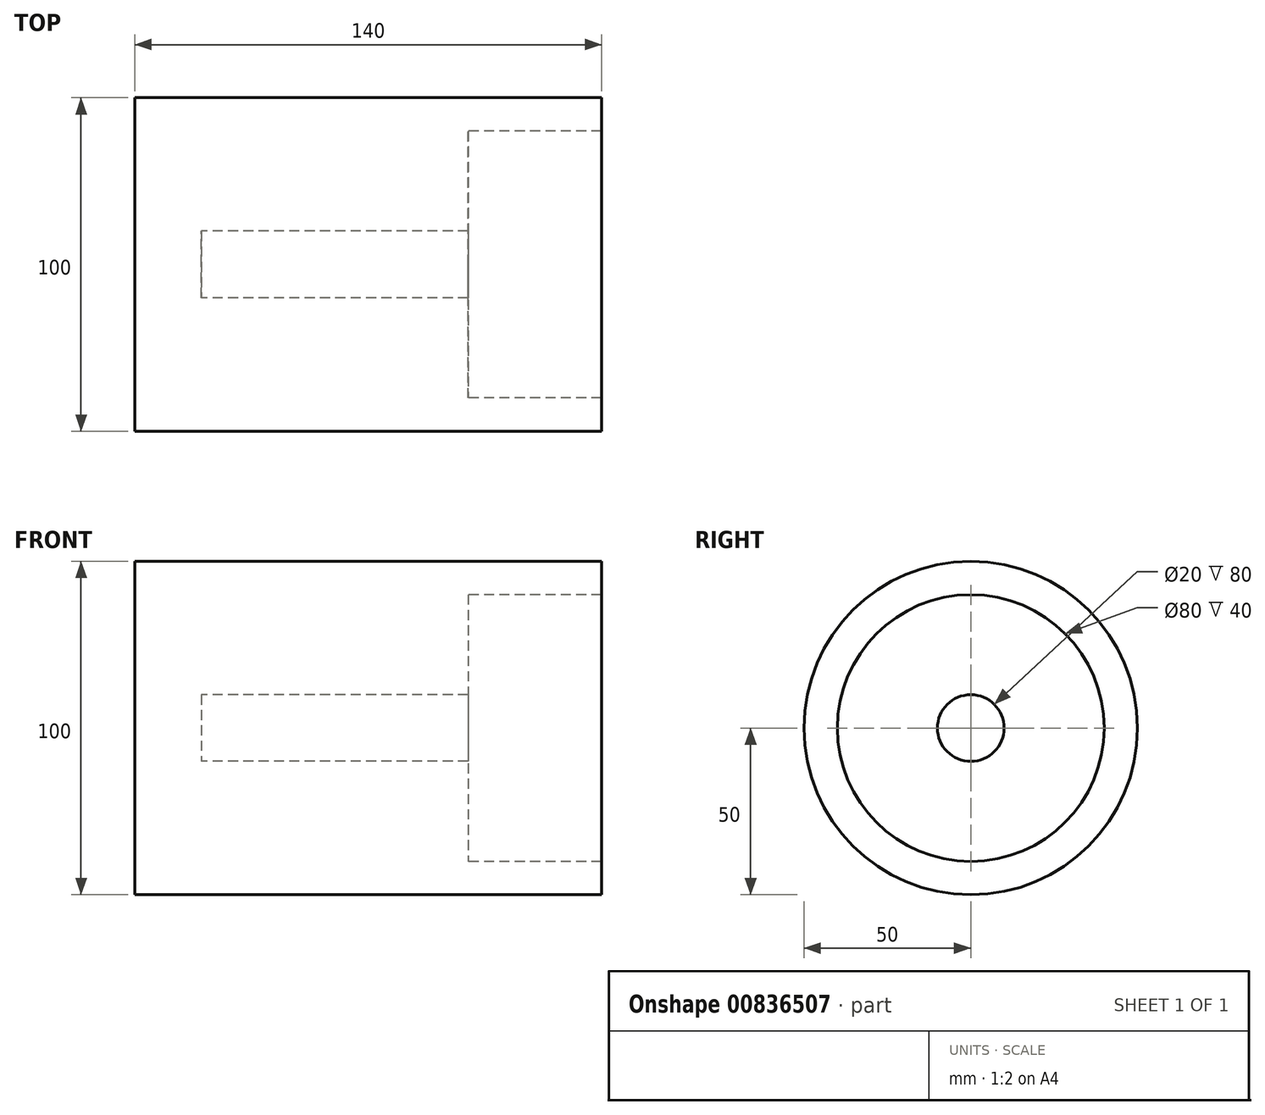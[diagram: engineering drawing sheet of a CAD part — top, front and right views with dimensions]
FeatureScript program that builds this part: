
annotation { "Feature Type Name" : "Feature", "Feature Type Description" : "" }
export const myFeature = defineFeature(function(context is Context, id is Id, definition is map)
    precondition{}
    {
        {
            var Q0;
            Q0=qCreatedBy(makeId("Top.planeOp"),FACE);
            var sketch = newSketch(context, id + "F0", { "sketchPlane" : qUnion([Q0])});
            skLineSegment(sketch, "E0", {"start": v(-70, 0) * mm, "end": v(-70, 50) * mm});
            skLineSegment(sketch, "E1", {"start": v(-70, 50) * mm, "end": v(70, 50) * mm});
            skLineSegment(sketch, "E2", {"start": v(70, 50) * mm, "end": v(70, 40) * mm});
            skLineSegment(sketch, "E3", {"start": v(70, 40) * mm, "end": v(30, 40) * mm});
            skLineSegment(sketch, "E4", {"start": v(30, 40) * mm, "end": v(30, 10) * mm});
            skLineSegment(sketch, "E5", {"start": v(30, 10) * mm, "end": v(-50, 10) * mm});
            skLineSegment(sketch, "E6", {"start": v(-50, 10) * mm, "end": v(-50, 0) * mm});
            skLineSegment(sketch, "E7", {"start": v(-70, 0) * mm, "end": v(-50, 0) * mm});
            skSolve(sketch);
        }
        {
            var Q0;
            Q0=makeQuery(id+"F0.imprint","IMPRINT",FACE,{"disambiguationData":[TD([[makeQuery(id+"F0.imprint","IMPRINT",EDGE,{"derivedFrom":sQuery(id+"F0.wireOp",EDGE,"E0")}),-1.0]])]});
            var Q1;
            Q1=sQuery(id+"F0.wireOp",EDGE,"E7");
            revolve(context, id + "F1", {"surfaceOperationType" : NewSurfaceOperationType.NEW, "entities" : qUnion([Q0]), "axis" : qUnion([Q1]), "revolveType" : RevolveType.FULL});
        }
    });
